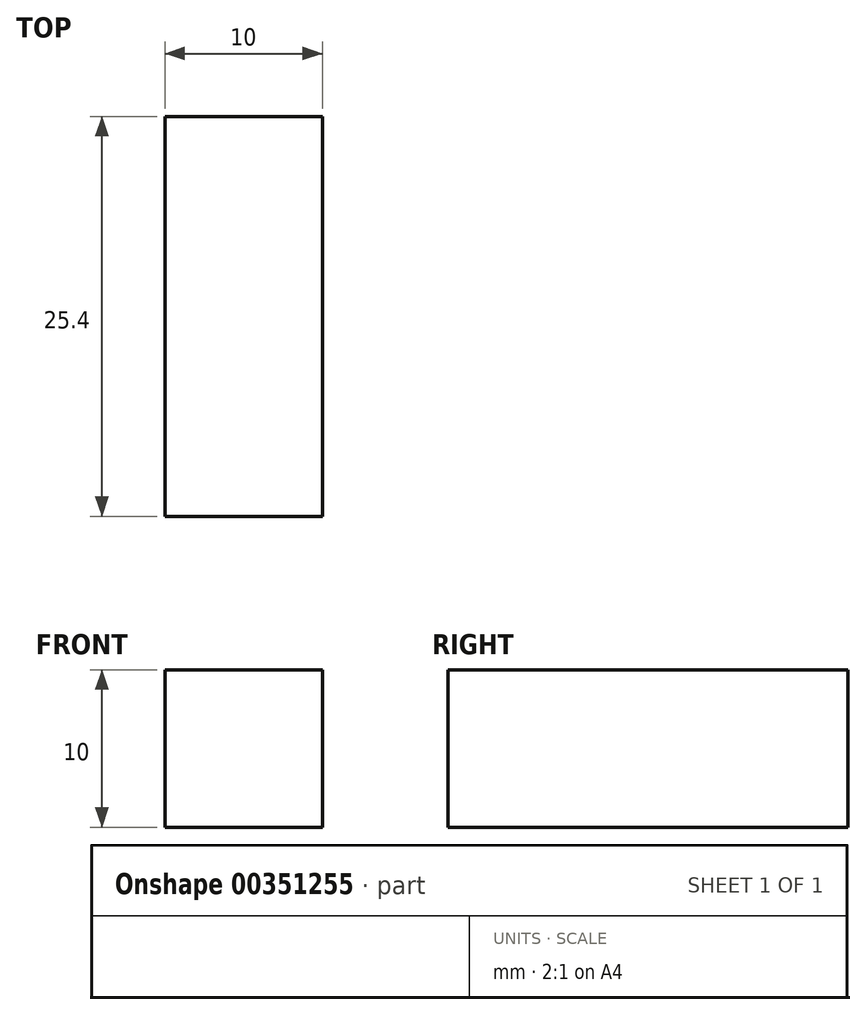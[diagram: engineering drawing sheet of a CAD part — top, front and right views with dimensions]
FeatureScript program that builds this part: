
annotation { "Feature Type Name" : "Feature", "Feature Type Description" : "" }
export const myFeature = defineFeature(function(context is Context, id is Id, definition is map)
    precondition{}
    {
        {
            var Q0;
            Q0=qCreatedBy(makeId("Right.planeOp"),FACE);
            var sketch = newSketch(context, id + "F0", { "sketchPlane" : qUnion([Q0])});
            skLineSegment(sketch, "E0.bottom", {"start": v(-12.33, -2.2) * mm, "end": v(13.07, -2.2) * mm});
            skLineSegment(sketch, "E0.top", {"start": v(-12.33, -12.2) * mm, "end": v(13.07, -12.2) * mm});
            skLineSegment(sketch, "E0.left", {"start": v(-12.33, -2.2) * mm, "end": v(-12.33, -12.2) * mm});
            skLineSegment(sketch, "E0.right", {"start": v(13.07, -2.2) * mm, "end": v(13.07, -12.2) * mm});
            skSolve(sketch);
        }
        {
            var Q0;
            Q0 = qSketchRegion(id + "F0", true);
            extrude(context, id + "F1", {"entities" : qUnion([Q0]), "depth" : 10 * mm});
        }
    });
